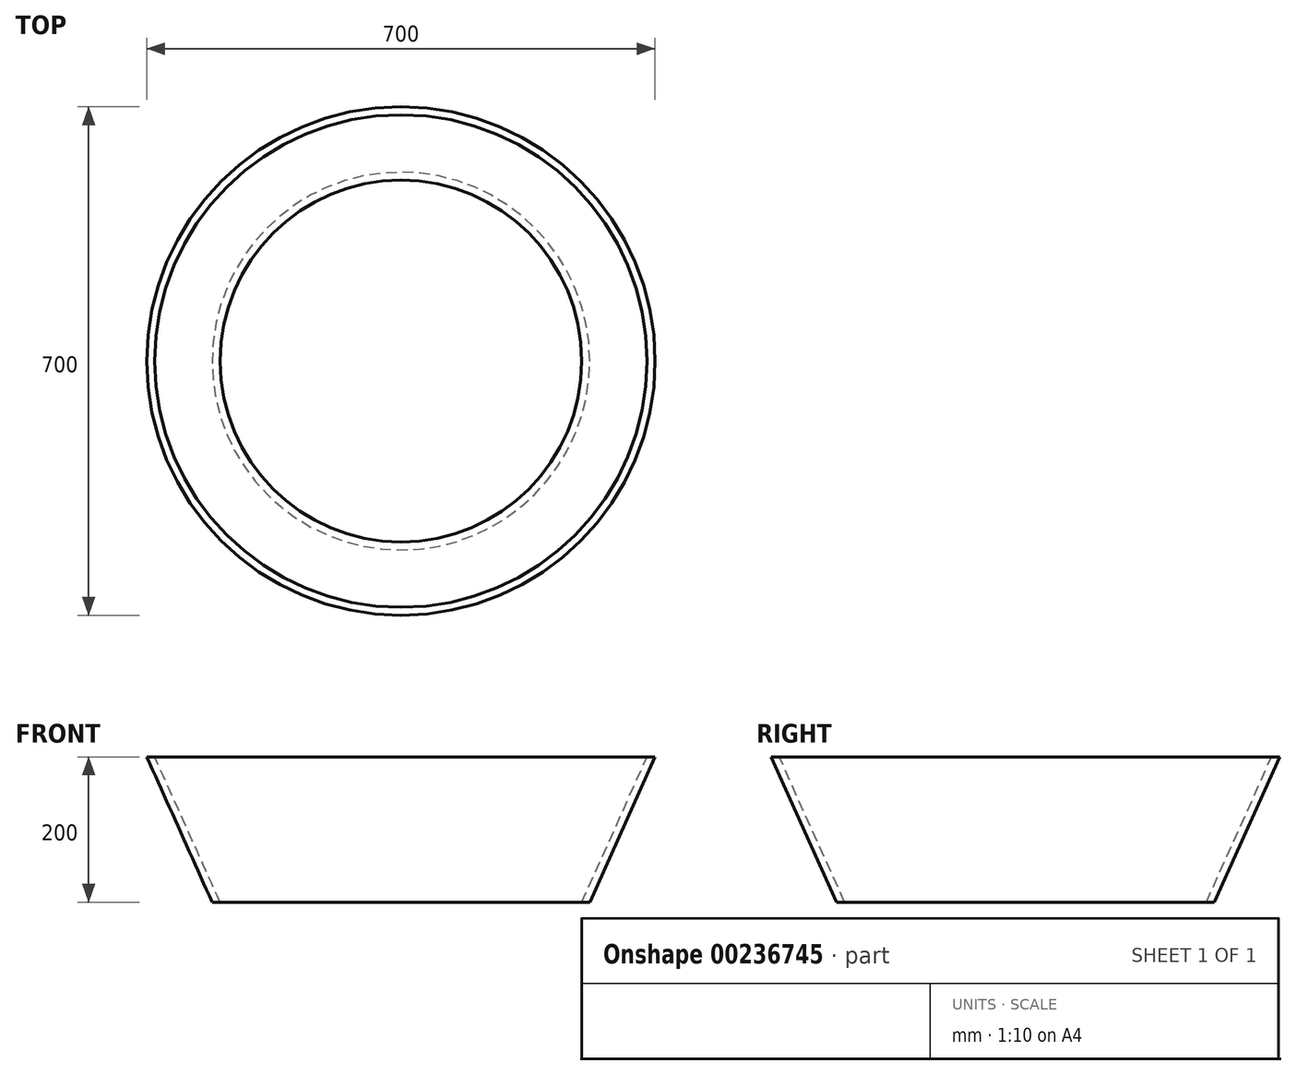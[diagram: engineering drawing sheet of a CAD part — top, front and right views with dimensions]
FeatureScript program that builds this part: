
annotation { "Feature Type Name" : "Feature", "Feature Type Description" : "" }
export const myFeature = defineFeature(function(context is Context, id is Id, definition is map)
    precondition{}
    {
        {
            var Q0;
            Q0=qCreatedBy(makeId("Front.planeOp"),FACE);
            var sketch = newSketch(context, id + "F0", { "sketchPlane" : qUnion([Q0])});
            skLineSegment(sketch, "E0", {"start": v(249.03, 0) * mm, "end": v(339.03, 200) * mm});
            skLineSegment(sketch, "E1", {"start": v(0, 0) * mm, "end": v(0, 273.55) * mm, "construction": true});
            skLineSegment(sketch, "E2", {"start": v(350, 200) * mm, "end": v(260, 0) * mm});
            skLineSegment(sketch, "E3", {"start": v(350, 200) * mm, "end": v(339.03, 200) * mm});
            skLineSegment(sketch, "E4", {"start": v(260, 0) * mm, "end": v(249.03, 0) * mm});
            skSolve(sketch);
        }
        {
            var Q0;
            Q0=makeQuery(id+"F0.imprint","IMPRINT",FACE,{"disambiguationData":[TD([[makeQuery(id+"F0.imprint","IMPRINT",EDGE,{"derivedFrom":sQuery(id+"F0.wireOp",EDGE,"E0")}),-1.0]])]});
            var Q1;
            Q1=sQuery(id+"F0.wireOp",EDGE,"E1");
            revolve(context, id + "F1", {"surfaceOperationType" : NewSurfaceOperationType.NEW, "entities" : qUnion([Q0]), "axis" : qUnion([Q1]), "revolveType" : RevolveType.FULL});
        }
    });
